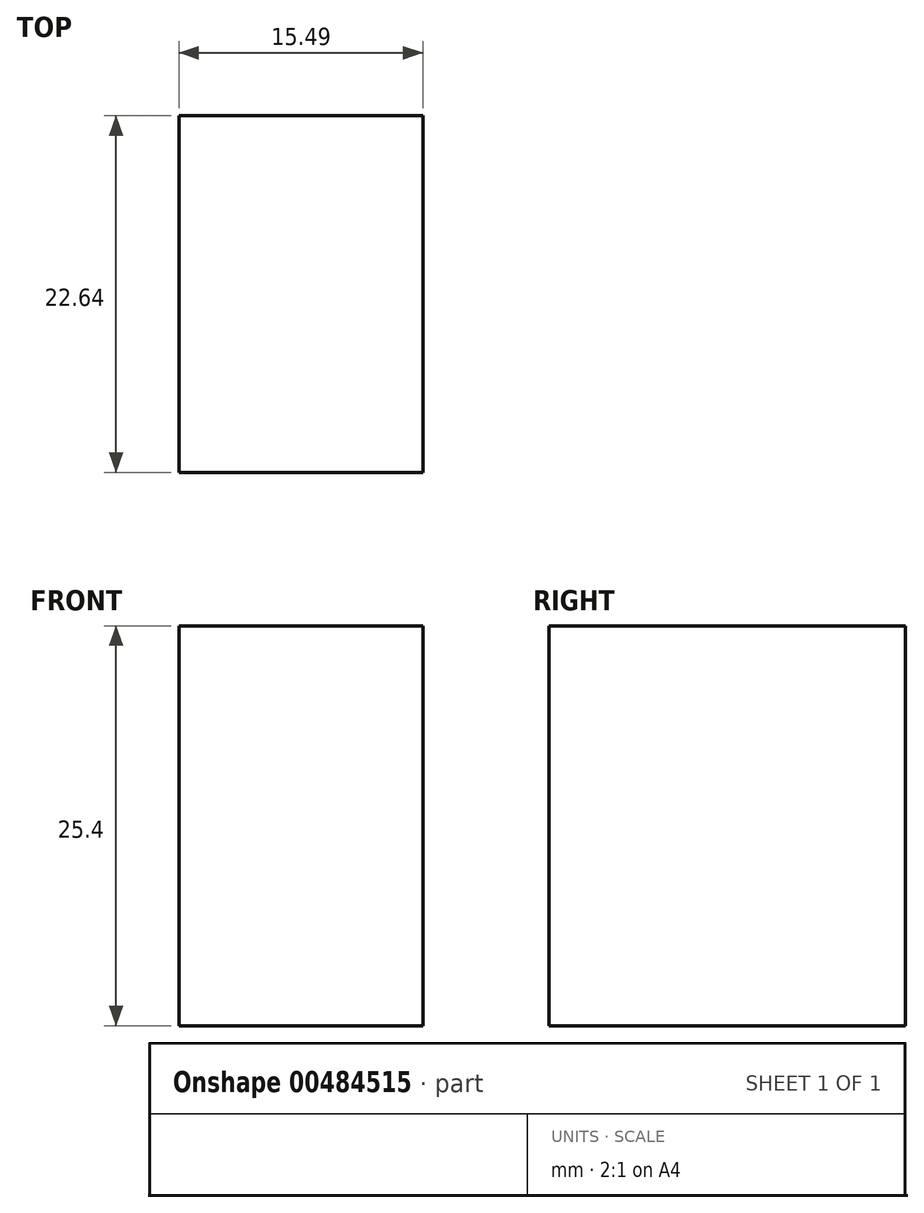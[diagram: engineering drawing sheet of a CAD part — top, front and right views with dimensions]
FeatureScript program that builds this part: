
annotation { "Feature Type Name" : "Feature", "Feature Type Description" : "" }
export const myFeature = defineFeature(function(context is Context, id is Id, definition is map)
    precondition{}
    {
        {
            var Q0;
            Q0=qCreatedBy(makeId("Top.planeOp"),FACE);
            var sketch = newSketch(context, id + "F0", { "sketchPlane" : qUnion([Q0])});
            skLineSegment(sketch, "E0.bottom", {"start": v(-5.68, -7.6) * mm, "end": v(9.81, -7.6) * mm});
            skLineSegment(sketch, "E0.top", {"start": v(-5.68, 15.04) * mm, "end": v(9.81, 15.04) * mm});
            skLineSegment(sketch, "E0.left", {"start": v(-5.68, -7.6) * mm, "end": v(-5.68, 15.04) * mm});
            skLineSegment(sketch, "E0.right", {"start": v(9.81, -7.6) * mm, "end": v(9.81, 15.04) * mm});
            skSolve(sketch);
        }
        {
            var Q0;
            Q0=makeQuery(id+"F0.imprint","IMPRINT",FACE,{"disambiguationData":[TD([[makeQuery(id+"F0.imprint","IMPRINT",EDGE,{"derivedFrom":sQuery(id+"F0.wireOp",EDGE,"E0.bottom")}),1.0]])]});
            extrude(context, id + "F1", {"entities" : qUnion([Q0]), "depth" : 25.4 * mm});
        }
    });
